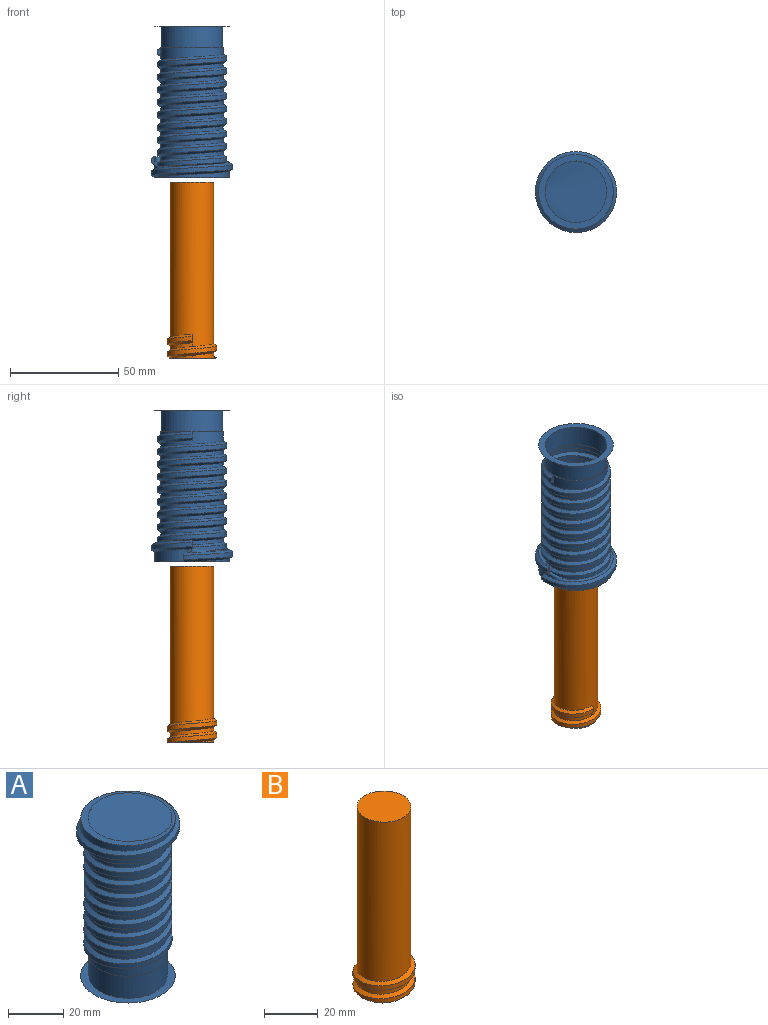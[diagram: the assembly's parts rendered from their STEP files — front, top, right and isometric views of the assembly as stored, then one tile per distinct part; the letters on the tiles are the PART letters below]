
ASSEMBLY  parts=2 mates=1
PART A: 17 faces, bbox 106.2x112x140.7 mm
  f0: cylinder r=17.2mm len=34.4mm, axis (0,0,1), area 521.9mm2, adj f1,f2,f3,f4,f5
  f1: plane 72.8x70.3mm, normal (0,-1,0), area 4.5mm2, adj f0,f2,f5,f6
  f2: bspline ~43.19x37.4mm, area 210.5mm2, adj f0,f1,f4,f6
  f3: plane 34.4x34.4mm, normal (0,0,1), area 929.4mm2, adj f0
  f4: plane 4.01x1.48mm, normal (-0.21,0.98,0), area 4.5mm2, adj f0,f2,f5,f6
  f5: bspline ~43.19x37.4mm, area 210.5mm2, adj f0,f1,f4,f6
  f6: cylinder r=18.7mm len=37.4mm, axis (0,0,1), area 243mm2, adj f1,f2,f4,f5
  f7: plane 29x29mm, normal (0,0,1), area 27mm2, adj f8,f9
  f8: cylinder r=14.5mm len=60mm, axis (0,0,1), area 1282.9mm2, adj f7,f10,f11,f12,f13
  f9: cylinder r=14.2mm len=28.4mm, axis (0,0,1), area 892.2mm2, adj f7,f14
  f10: plane 31.39x31.09mm, normal (0,0,-1), area 734.5mm2, adj f8,f11,f13,f15
  f11: bspline ~61.9x36.95mm, area 1782.4mm2, adj f8,f10,f12,f15
  f12: plane 4x1.5mm, normal (0,1,0), area 4.5mm2, adj f8,f11,f13,f15
  f13: bspline ~58.03x36.95mm, area 1676.1mm2, adj f8,f10,f12,f15
  f14: plane 103.2x103.2mm, normal (0,0,-1), area 295.9mm2, adj f9,f16
  f15: cylinder r=16mm len=59mm, axis (0,0,1), area 2436.9mm2, adj f10,f11,f12,f13
  f16: cylinder r=17.2mm len=34.4mm, axis (0,0,1), area 0mm2, adj f14
PART B: 10 faces, bbox 23.2x26.8x82.9 mm
  f0: cylinder r=10mm len=20mm, axis (0,0,-1), area 116.7mm2, adj f1,f2,f4,f6,f7,f8
  f1: cylinder r=10mm len=9.66mm, axis (0,0,-1), area 7.9mm2, adj f0,f7,f8
  f2: cylinder r=10mm len=75.8mm, axis (0,0,-1), area 4580.4mm2, adj f0,f3,f6,f9
  f3: plane 4x1.5mm, normal (0,1,0), area 4.5mm2, adj f2,f5,f6,f7
  f4: plane 1.49x1.01mm, normal (0.99,0.16,0), area 0.7mm2, adj f0,f6,f8
  f5: cylinder r=11.5mm len=23mm, axis (0,0,-1), area 223.4mm2, adj f3,f6,f7,f8
  f6: bspline ~26.56x23mm, area 210.5mm2, adj f0,f2,f3,f4,f5
  f7: bspline ~26.56x23mm, area 158.4mm2, adj f0,f1,f3,f5,f8
  f8: plane 22.05x21.73mm, normal (0,0,-1), area 357.6mm2, adj f0,f1,f4,f5,f7
  f9: plane 20x20mm, normal (0,0,1), area 314.2mm2, adj f2
PLACE A rot(axis=(0,1,0),180deg) t=(128.17,70.9,181.41)mm fixed
PLACE B rot(axis=(0,0,-1),89deg) t=(-41.85,20.61,35.4)mm
MATE cylindrical B.f0 <-> A.f15  axis (0,0,-1) through (-42.73,70.9,119.4)mm
